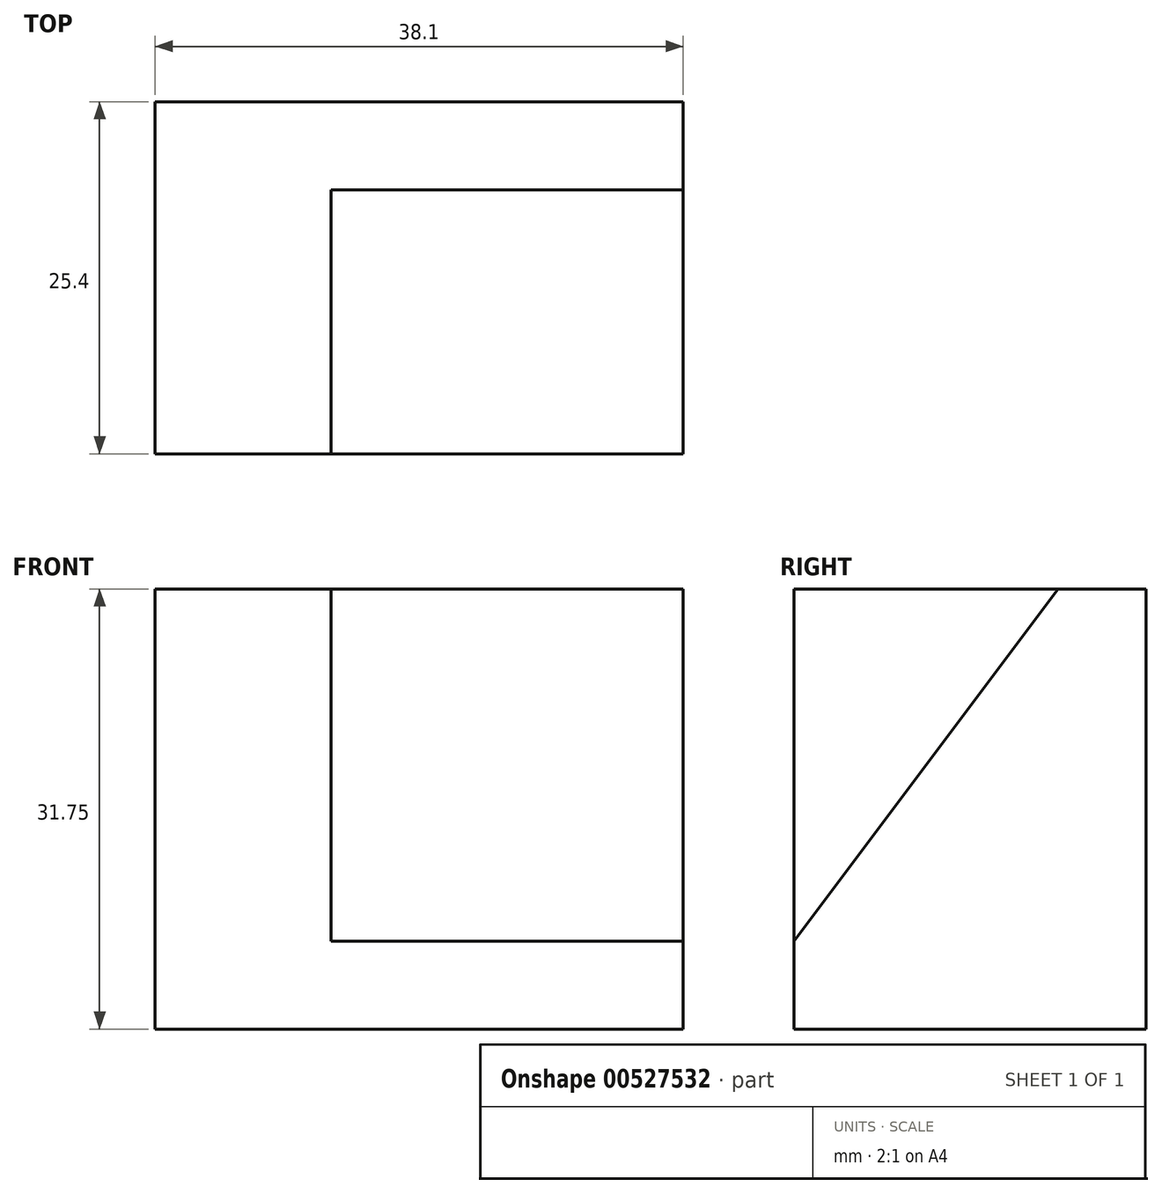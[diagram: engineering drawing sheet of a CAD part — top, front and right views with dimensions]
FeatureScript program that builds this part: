
annotation { "Feature Type Name" : "Feature", "Feature Type Description" : "" }
export const myFeature = defineFeature(function(context is Context, id is Id, definition is map)
    precondition{}
    {
        {
            var Q0;
            Q0=qCreatedBy(makeId("Front.planeOp"),FACE);
            var sketch = newSketch(context, id + "F0", { "sketchPlane" : qUnion([Q0])});
            skLineSegment(sketch, "E0", {"start": v(0, 0) * mm, "end": v(38.1, 0) * mm});
            skLineSegment(sketch, "E1", {"start": v(38.1, 0) * mm, "end": v(38.1, 31.75) * mm});
            skLineSegment(sketch, "E2", {"start": v(38.1, 31.75) * mm, "end": v(0, 31.75) * mm});
            skLineSegment(sketch, "E3", {"start": v(0, 31.75) * mm, "end": v(0, 0) * mm});
            skSolve(sketch);
        }
        {
            var Q0;
            Q0 = qSketchRegion(id + "F0", true);
            extrude(context, id + "F1", {"entities" : qUnion([Q0]), "depth" : 25.4 * mm, "offsetDistance" : 25.4 * mm});
        }
        {
            var Q0;
            Q0=makeQuery(id+"F1.opExtrude","SWEPT_FACE",FACE,{"disambiguationData":[OSD([sQuery(id+"F0.wireOp",EDGE,"E1")])]});
            var sketch = newSketch(context, id + "F2", { "sketchPlane" : qUnion([Q0])});
            skLineSegment(sketch, "E4", {"start": v(-25.4, 0) * mm, "end": v(-25.4, 6.35) * mm});
            skLineSegment(sketch, "E5", {"start": v(-25.4, 6.35) * mm, "end": v(-6.35, 31.75) * mm});
            skLineSegment(sketch, "E6", {"start": v(-6.35, 31.75) * mm, "end": v(0, 31.75) * mm});
            skSolve(sketch);
        }
        {
            var Q0;
            Q0 = qSketchRegion(id + "F2", true);
            var Q1;
            {var subQ0=sQuery(id+"F2.wireOp",EDGE,"E5");Q1=makeQuery(id+"F2.imprint","IMPRINT",FACE,{"disambiguationData":[TD([[makeQuery(id+"F2.imprint","IMPRINT",EDGE,{"derivedFrom":subQ0}),1.0]])]});}
            extrude(context, id + "F3", {"entities" : qUnion([Q0, Q1]), "operationType" : NewBodyOperationType.REMOVE, "oppositeDirection" : true, "depth" : 25.4 * mm, "offsetDistance" : 25.4 * mm});
        }
    });
